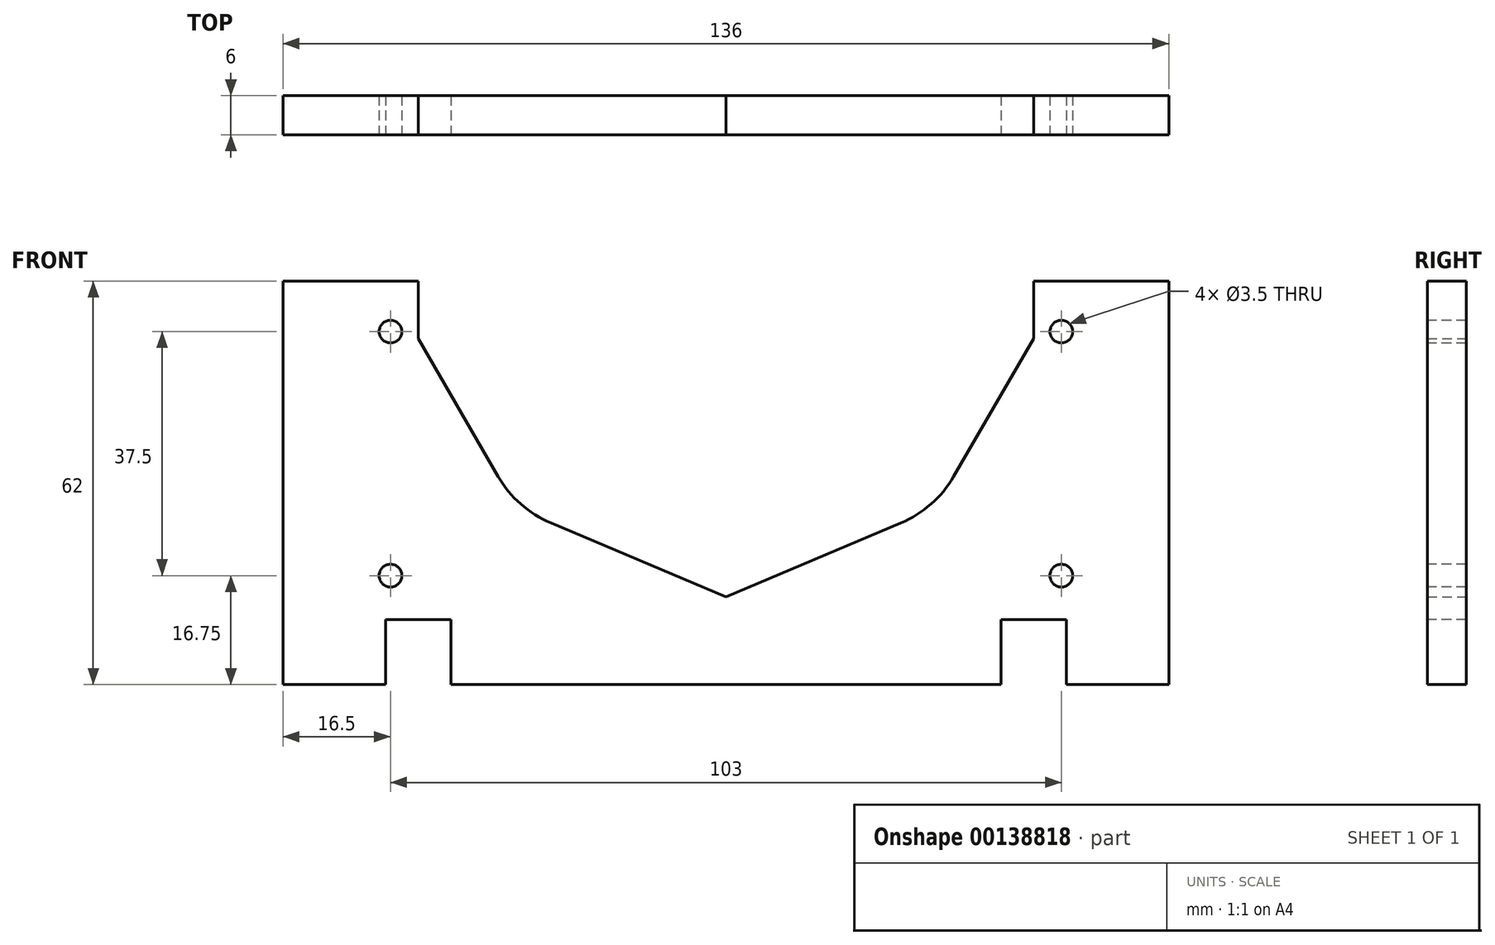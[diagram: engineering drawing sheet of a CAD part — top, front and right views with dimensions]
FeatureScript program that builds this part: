
annotation { "Feature Type Name" : "Feature", "Feature Type Description" : "" }
export const myFeature = defineFeature(function(context is Context, id is Id, definition is map)
    precondition{}
    {
        {
            var Q0;
            Q0=qCreatedBy(makeId("Front.planeOp"),FACE);
            var sketch = newSketch(context, id + "F0", { "sketchPlane" : qUnion([Q0])});
            skLineSegment(sketch, "E0", {"start": v(0, 0) * mm, "end": v(0, 62) * mm, "construction": true});
            skLineSegment(sketch, "E1", {"start": v(0, 0) * mm, "end": v(-68, 0) * mm});
            skLineSegment(sketch, "E2", {"start": v(-68, 0) * mm, "end": v(-68, 62) * mm});
            skLineSegment(sketch, "E3", {"start": v(-68, 62) * mm, "end": v(-47.25, 62) * mm});
            skLineSegment(sketch, "E4", {"start": v(-47.25, 62) * mm, "end": v(-47.25, 53.15) * mm});
            skLineSegment(sketch, "E5.MirrorCS", {"start": v(0, 0) * mm, "end": v(68, 0) * mm});
            skLineSegment(sketch, "E6.MirrorCS", {"start": v(68, 0) * mm, "end": v(68, 62) * mm});
            skLineSegment(sketch, "E7.MirrorCS", {"start": v(68, 62) * mm, "end": v(47.25, 62) * mm});
            skLineSegment(sketch, "E8.MirrorCS", {"start": v(47.25, 62) * mm, "end": v(47.25, 53.15) * mm});
            skLineSegment(sketch, "E9", {"start": v(-47.25, 53.15) * mm, "end": v(-47.25, 0) * mm, "construction": true});
            skLineSegment(sketch, "E10", {"start": v(0, 13.5) * mm, "end": v(-68, 13.5) * mm, "construction": true});
            skArc(sketch, "E11", {"start": v(-34.95, 31.96) * mm, "mid": v(-31.49, 27.74) * mm, "end": v(-26.86, 24.84) * mm});
            skPoint(sketch, "E11.second.point", {"position": v(-13.55, 24.87) * mm});
            skLineSegment(sketch, "E12", {"start": v(-47.25, 53.15) * mm, "end": v(-34.95, 31.96) * mm});
            skLineSegment(sketch, "E13", {"start": v(0, 13.5) * mm, "end": v(-26.86, 24.84) * mm});
            skPoint(sketch, "E14.MirrorCS.end.orphan", {"position": v(0, 13.5) * mm});
            skPoint(sketch, "E14.MirrorCS.start.orphan", {"position": v(47.25, 53.15) * mm});
            skLineSegment(sketch, "E15.MirrorCS", {"start": v(47.25, 53.15) * mm, "end": v(34.95, 31.96) * mm});
            skArc(sketch, "E16.MirrorCS", {"start": v(34.95, 31.96) * mm, "mid": v(31.49, 27.74) * mm, "end": v(26.86, 24.84) * mm});
            skLineSegment(sketch, "E17.MirrorCS", {"start": v(0, 13.5) * mm, "end": v(26.86, 24.84) * mm});
            skSolve(sketch);
        }
        {
            var Q0;
            Q0=qSketchRegion(id+"F0",true);
            extrude(context, id + "F1", {"entities" : qUnion([Q0]), "depth" : 6 * mm});
        }
        {
            var Q0;
            Q0=makeQuery(id+"F1.opExtrude","CAP_FACE",FACE,{"disambiguationData":[OSD([sQuery(id+"F0.wireOp",EDGE,"E1"),sQuery(id+"F0.wireOp",EDGE,"E2"),sQuery(id+"F0.wireOp",EDGE,"E3"),sQuery(id+"F0.wireOp",EDGE,"E4"),sQuery(id+"F0.wireOp",EDGE,"E5.MirrorCS"),sQuery(id+"F0.wireOp",EDGE,"E6.MirrorCS"),sQuery(id+"F0.wireOp",EDGE,"E7.MirrorCS"),sQuery(id+"F0.wireOp",EDGE,"E8.MirrorCS"),sQuery(id+"F0.wireOp",EDGE,"E11"),sQuery(id+"F0.wireOp",EDGE,"E12"),sQuery(id+"F0.wireOp",EDGE,"E13"),sQuery(id+"F0.wireOp",EDGE,"E15.MirrorCS"),sQuery(id+"F0.wireOp",EDGE,"E16.MirrorCS"),sQuery(id+"F0.wireOp",EDGE,"E17.MirrorCS")])],"isStart":false});
            var sketch = newSketch(context, id + "F2", { "sketchPlane" : qUnion([Q0])});
            skCircle(sketch, "E18", {"center": v(-51.5, 54.25) * mm, "radius": 1.75 * mm});
            skCircle(sketch, "E19", {"center": v(-51.5, 16.75) * mm, "radius": 1.75 * mm});
            skCircle(sketch, "E20.MirrorC", {"center": v(51.5, 54.25) * mm, "radius": 1.75 * mm});
            skCircle(sketch, "E21.MirrorC", {"center": v(51.5, 16.75) * mm, "radius": 1.75 * mm});
            skSolve(sketch);
        }
        {
            var Q0;
            Q0 = qSketchRegion(id + "F2", true);
            extrude(context, id + "F3", {"entities" : qUnion([Q0]), "operationType" : NewBodyOperationType.REMOVE, "endBound" : BoundingType.THROUGH_ALL, "oppositeDirection" : true, "depth" : 25 * mm});
        }
        {
            var Q0;
            Q0=makeQuery(id+"F1.opExtrude","CAP_FACE",FACE,{"disambiguationData":[OSD([sQuery(id+"F0.wireOp",EDGE,"E1"),sQuery(id+"F0.wireOp",EDGE,"E2"),sQuery(id+"F0.wireOp",EDGE,"E3"),sQuery(id+"F0.wireOp",EDGE,"E4"),sQuery(id+"F0.wireOp",EDGE,"E5.MirrorCS"),sQuery(id+"F0.wireOp",EDGE,"E6.MirrorCS"),sQuery(id+"F0.wireOp",EDGE,"E7.MirrorCS"),sQuery(id+"F0.wireOp",EDGE,"E8.MirrorCS"),sQuery(id+"F0.wireOp",EDGE,"E11"),sQuery(id+"F0.wireOp",EDGE,"E12"),sQuery(id+"F0.wireOp",EDGE,"E13"),sQuery(id+"F0.wireOp",EDGE,"E15.MirrorCS"),sQuery(id+"F0.wireOp",EDGE,"E16.MirrorCS"),sQuery(id+"F0.wireOp",EDGE,"E17.MirrorCS")])],"isStart":false});
            var sketch = newSketch(context, id + "F4", { "sketchPlane" : qUnion([Q0])});
            skLineSegment(sketch, "E22.bottom", {"start": v(-52.25, 0) * mm, "end": v(-42.25, 0) * mm});
            skLineSegment(sketch, "E22.top", {"start": v(-52.25, 10) * mm, "end": v(-42.25, 10) * mm});
            skLineSegment(sketch, "E22.left", {"start": v(-52.25, 0) * mm, "end": v(-52.25, 10) * mm});
            skLineSegment(sketch, "E22.right", {"start": v(-42.25, 0) * mm, "end": v(-42.25, 10) * mm});
            skLineSegment(sketch, "E23.MirrorCS", {"start": v(42.25, 0) * mm, "end": v(42.25, 10) * mm});
            skLineSegment(sketch, "E24.MirrorCS", {"start": v(52.25, 10) * mm, "end": v(42.25, 10) * mm});
            skLineSegment(sketch, "E25.MirrorCS", {"start": v(52.25, 0) * mm, "end": v(52.25, 10) * mm});
            skLineSegment(sketch, "E26.MirrorCS", {"start": v(52.25, 0) * mm, "end": v(42.25, 0) * mm});
            skSolve(sketch);
        }
        {
            var Q0;
            Q0 = qSketchRegion(id + "F4", true);
            extrude(context, id + "F5", {"entities" : qUnion([Q0]), "operationType" : NewBodyOperationType.REMOVE, "endBound" : BoundingType.THROUGH_ALL, "oppositeDirection" : true, "depth" : 25 * mm});
        }
    });
